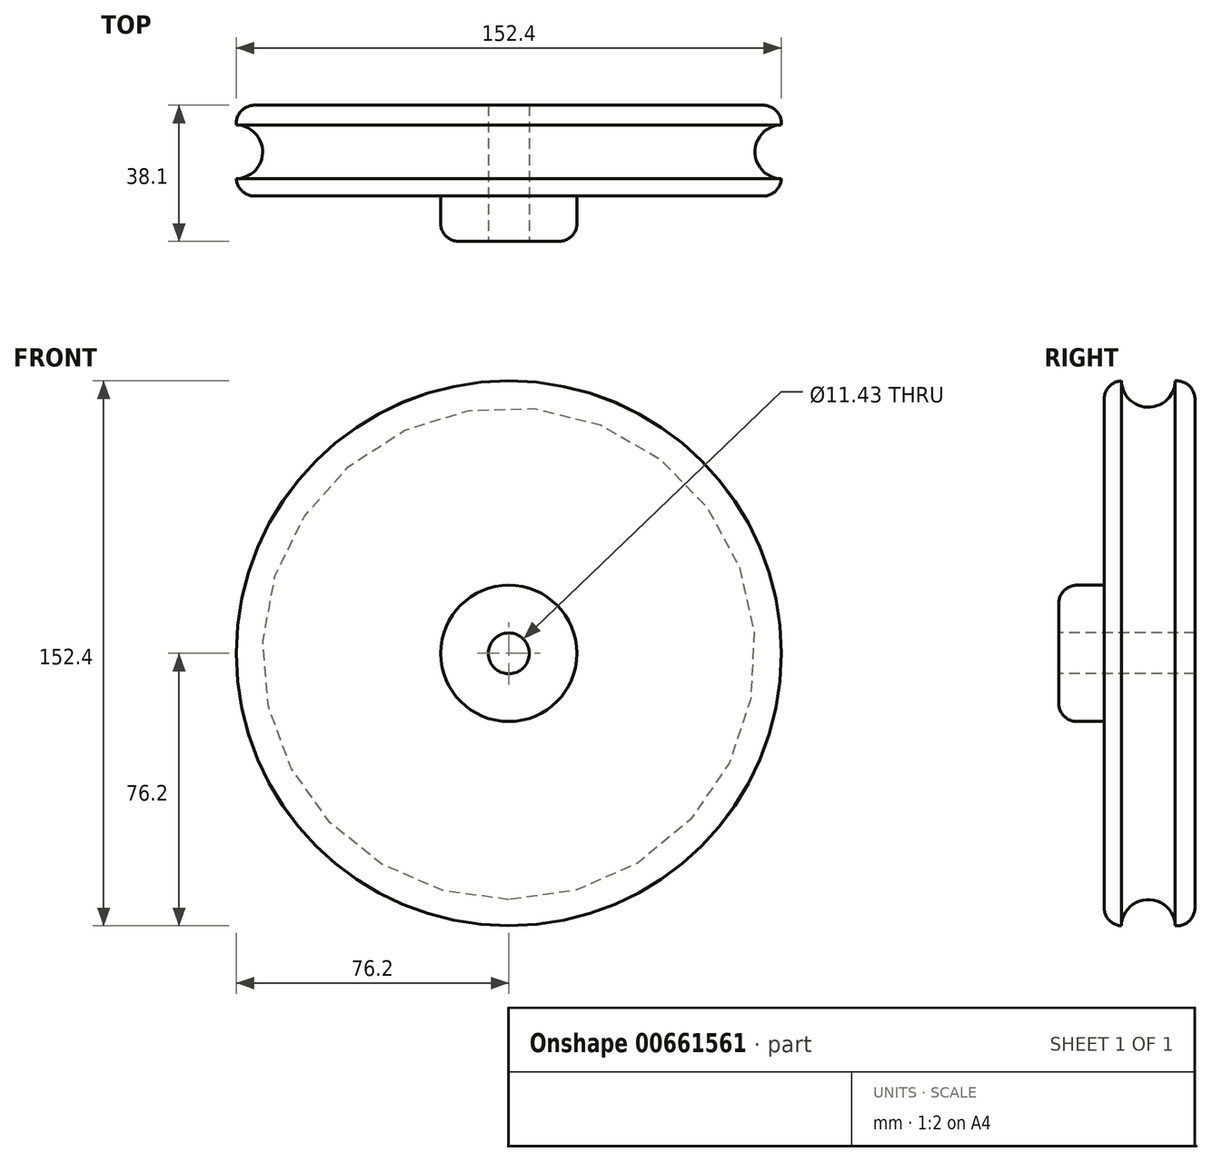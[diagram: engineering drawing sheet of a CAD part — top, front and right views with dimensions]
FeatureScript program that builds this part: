
annotation { "Feature Type Name" : "Feature", "Feature Type Description" : "" }
export const myFeature = defineFeature(function(context is Context, id is Id, definition is map)
    precondition{}
    {
        {
            var Q0;
            Q0=qCreatedBy(makeId("Front.planeOp"),FACE);
            var sketch = newSketch(context, id + "F0", { "sketchPlane" : qUnion([Q0])});
            skCircle(sketch, "E0", {"center": v(0, 0) * mm, "radius": 76.2 * mm});
            skSolve(sketch);
        }
        {
            var Q0;
            Q0=makeQuery(id+"F0.imprint","IMPRINT",FACE,{"disambiguationData":[TD([[makeQuery(id+"F0.imprint","IMPRINT",EDGE,{"derivedFrom":sQuery(id+"F0.wireOp",EDGE,"E0")}),1.0]])]});
            extrude(context, id + "F1", {"entities" : qUnion([Q0]), "depth" : 25.4 * mm, "offsetDistance" : 25.4 * mm});
        }
        {
            var Q0;
            Q0=makeQuery(id+"F1.opExtrude","CAP_FACE",FACE,{"disambiguationData":[OSD([sQuery(id+"F0.wireOp",EDGE,"E0")])],"isStart":false});
            var sketch = newSketch(context, id + "F2", { "sketchPlane" : qUnion([Q0])});
            skCircle(sketch, "E1", {"center": v(0, 0) * mm, "radius": 19.05 * mm});
            skSolve(sketch);
        }
        {
            var Q0;
            Q0 = qSketchRegion(id + "F2", true);
            extrude(context, id + "F3", {"entities" : qUnion([Q0]), "operationType" : NewBodyOperationType.ADD, "depth" : 12.7 * mm, "offsetDistance" : 25.4 * mm});
        }
        {
            var Q0;
            Q0=makeQuery(id+"F3.opExtrude","CAP_FACE",FACE,{"disambiguationData":[OSD([sQuery(id+"F2.wireOp",EDGE,"E1")])],"isStart":false});
            var sketch = newSketch(context, id + "F4", { "sketchPlane" : qUnion([Q0])});
            skPoint(sketch, "E2", {"position": v(0, 0) * mm});
            skSolve(sketch);
        }
        {
            var Q0;
            Q0=sQuery(id+"F4.wireOp",VERTEX,"E2");
            var Q1;
            Q1=makeQuery(id+"F1.opExtrude","SWEPT_BODY",BODY,{"disambiguationData":[OSD([sQuery(id+"F0.wireOp",EDGE,"E0")])]});
            hole(context, id + "F5", {"style" : HoleStyle.SIMPLE, "endStyle" : HoleEndStyle.THROUGH, "holeDiameter" : 11.43 * mm, "majorDiameter" : 6.35 * mm, "isTappedThrough" : true, "tappedDepth" : 12.7 * mm, "tapClearance" : 3, "locations" : qUnion([Q0]), "scope" : qUnion([Q1])});
        }
        {
            var Q0;
            Q0=makeQuery(id+"F1.opExtrude","CAP_EDGE",EDGE,{"disambiguationData":[OSD([sQuery(id+"F0.wireOp",EDGE,"E0")])],"isStart":false});
            var Q1;
            Q1=makeQuery(id+"F1.opExtrude","SWEPT_FACE",FACE,{"disambiguationData":[OSD([sQuery(id+"F0.wireOp",EDGE,"E0")])]});
            var Q2;
            Q2=makeQuery(id+"F3.opExtrude","CAP_EDGE",EDGE,{"disambiguationData":[OSD([sQuery(id+"F2.wireOp",EDGE,"E1")])],"isStart":false});
            fillet(context, id + "F6", {"entities" : qUnion([Q0, Q1, Q2]), "radius" : 5.08 * mm, "tangentPropagation" : true, "allowEdgeOverflow" : false});
        }
        {
            var Q0;
            Q0=qCreatedBy(makeId("Right.planeOp"),FACE);
            var sketch = newSketch(context, id + "F7", { "sketchPlane" : qUnion([Q0])});
            skCircle(sketch, "E3", {"center": v(-13.05, 76.4) * mm, "radius": 7.55 * mm});
            skSolve(sketch);
        }
        {
            var Q0;
            Q0=makeQuery(id+"F7.imprint","IMPRINT",FACE,{"disambiguationData":[TD([[makeQuery(id+"F7.imprint","IMPRINT",EDGE,{"derivedFrom":sQuery(id+"F7.wireOp",EDGE,"E3")}),1.0]])]});
            var Q1;
            Q1=makeQuery(id+"F1.opExtrude","SWEPT_FACE",FACE,{"disambiguationData":[OSD([sQuery(id+"F0.wireOp",EDGE,"E0")])]});
            revolve(context, id + "F8", {"operationType" : NewBodyOperationType.REMOVE, "entities" : qUnion([Q0]), "axis" : qUnion([Q1]), "revolveType" : RevolveType.FULL, "oppositeDirection" : true});
        }
    });
